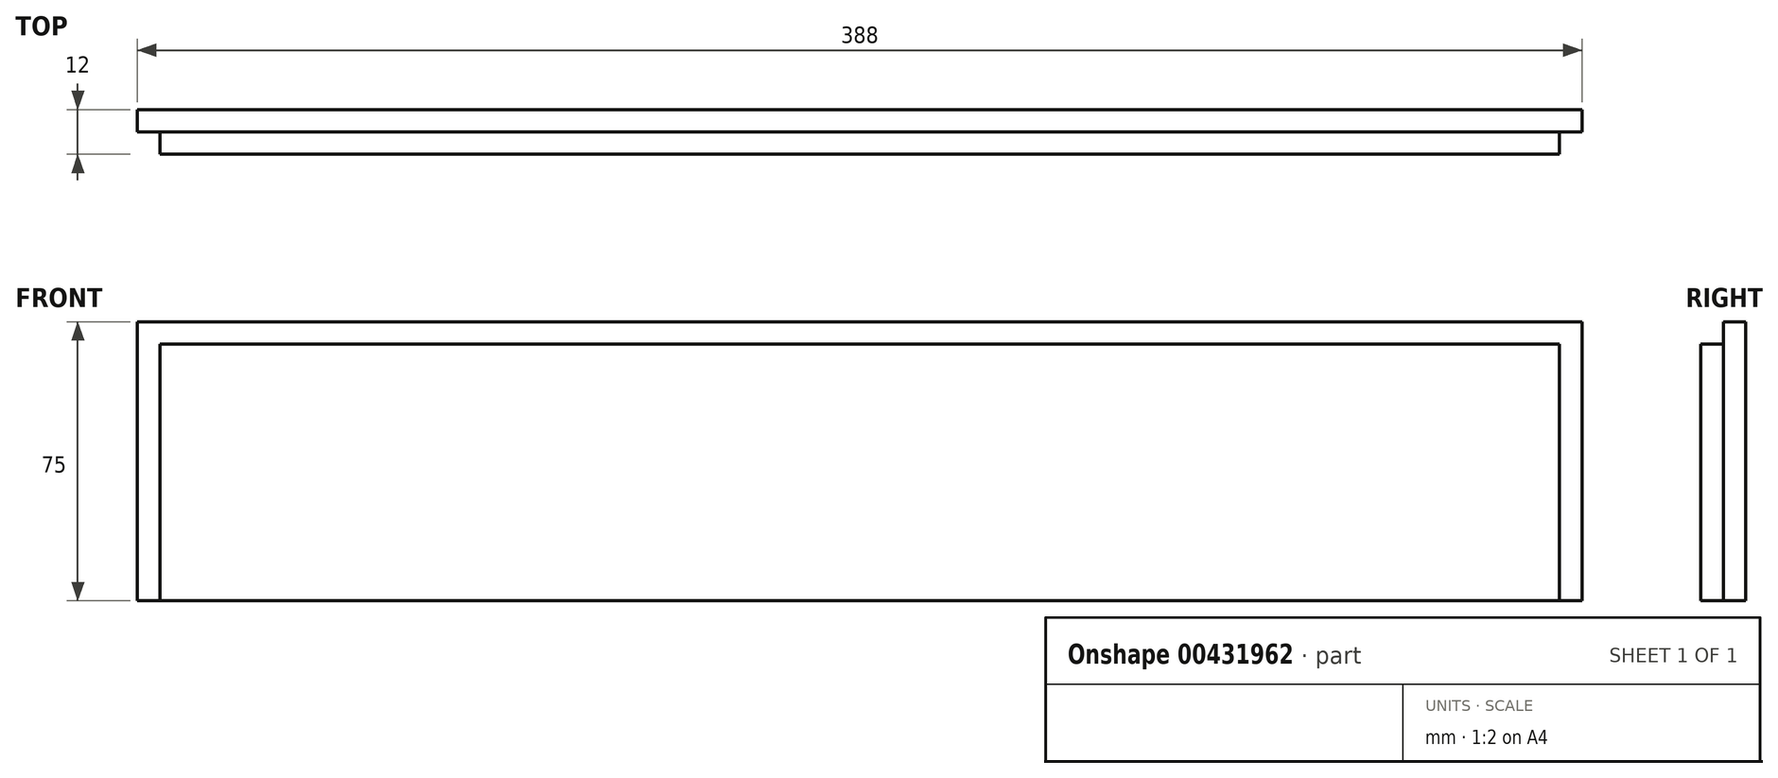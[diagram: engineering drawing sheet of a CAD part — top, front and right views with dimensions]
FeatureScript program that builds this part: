
annotation { "Feature Type Name" : "Feature", "Feature Type Description" : "" }
export const myFeature = defineFeature(function(context is Context, id is Id, definition is map)
    precondition{}
    {
        {
            var Q0;
            Q0=qCreatedBy(makeId("Front.planeOp"),FACE);
            var sketch = newSketch(context, id + "F0", { "sketchPlane" : qUnion([Q0])});
            skLineSegment(sketch, "E0.bottom", {"start": v(-183, 37.5) * mm, "end": v(205, 37.5) * mm});
            skLineSegment(sketch, "E0.top", {"start": v(-183, -37.5) * mm, "end": v(205, -37.5) * mm});
            skLineSegment(sketch, "E0.left", {"start": v(-183, 37.5) * mm, "end": v(-183, -37.5) * mm});
            skLineSegment(sketch, "E0.right", {"start": v(205, 37.5) * mm, "end": v(205, -37.5) * mm});
            skPoint(sketch, "E0.middle", {"position": v(11, 0) * mm});
            skSolve(sketch);
        }
        {
            var Q0;
            Q0=qSketchRegion(id+"F0",true);
            extrude(context, id + "F1", {"entities" : qUnion([Q0]), "depth" : 12 * mm, "offsetDistance" : 25 * mm});
        }
        {
            var Q0;
            Q0=makeQuery(id+"F1.opExtrude","CAP_FACE",FACE,{"disambiguationData":[OSD([sQuery(id+"F0.wireOp",EDGE,"E0.bottom"),sQuery(id+"F0.wireOp",EDGE,"E0.top"),sQuery(id+"F0.wireOp",EDGE,"E0.left"),sQuery(id+"F0.wireOp",EDGE,"E0.right")])],"isStart":false});
            var sketch = newSketch(context, id + "F2", { "sketchPlane" : qUnion([Q0])});
            skLineSegment(sketch, "E1.bottom", {"start": v(-183, 37.5) * mm, "end": v(-177, 37.5) * mm});
            skLineSegment(sketch, "E1.top", {"start": v(-183, -37.5) * mm, "end": v(-177, -37.5) * mm});
            skLineSegment(sketch, "E1.left", {"start": v(-183, 37.5) * mm, "end": v(-183, -37.5) * mm});
            skLineSegment(sketch, "E1.right", {"start": v(-177, 37.5) * mm, "end": v(-177, -37.5) * mm});
            skSolve(sketch);
        }
        {
            var Q0;
            Q0=qSketchRegion(id+"F2",true);
            extrude(context, id + "F3", {"entities" : qUnion([Q0]), "operationType" : NewBodyOperationType.REMOVE, "oppositeDirection" : true, "depth" : 6 * mm, "offsetDistance" : 25 * mm});
        }
        {
            var Q0;
            Q0=makeQuery(id+"F1.opExtrude","CAP_FACE",FACE,{"disambiguationData":[OSD([sQuery(id+"F0.wireOp",EDGE,"E0.bottom"),sQuery(id+"F0.wireOp",EDGE,"E0.top"),sQuery(id+"F0.wireOp",EDGE,"E0.left"),sQuery(id+"F0.wireOp",EDGE,"E0.right")])],"isStart":false});
            var sketch = newSketch(context, id + "F4", { "sketchPlane" : qUnion([Q0])});
            skLineSegment(sketch, "E2.bottom", {"start": v(205, 37.5) * mm, "end": v(199, 37.5) * mm});
            skLineSegment(sketch, "E2.top", {"start": v(205, -37.5) * mm, "end": v(199, -37.5) * mm});
            skLineSegment(sketch, "E2.left", {"start": v(205, 37.5) * mm, "end": v(205, -37.5) * mm});
            skLineSegment(sketch, "E2.right", {"start": v(199, 37.5) * mm, "end": v(199, -37.5) * mm});
            skSolve(sketch);
        }
        {
            var Q0;
            Q0=qSketchRegion(id+"F4",true);
            extrude(context, id + "F5", {"entities" : qUnion([Q0]), "operationType" : NewBodyOperationType.REMOVE, "oppositeDirection" : true, "depth" : 6 * mm, "offsetDistance" : 25 * mm});
        }
        {
            var Q0;
            Q0=makeQuery(id+"F1.opExtrude","CAP_FACE",FACE,{"disambiguationData":[OSD([sQuery(id+"F0.wireOp",EDGE,"E0.bottom"),sQuery(id+"F0.wireOp",EDGE,"E0.top"),sQuery(id+"F0.wireOp",EDGE,"E0.left"),sQuery(id+"F0.wireOp",EDGE,"E0.right")])],"isStart":false});
            var sketch = newSketch(context, id + "F6", { "sketchPlane" : qUnion([Q0])});
            skLineSegment(sketch, "E3.bottom", {"start": v(-177, 37.5) * mm, "end": v(199, 37.5) * mm});
            skLineSegment(sketch, "E3.top", {"start": v(-177, 31.5) * mm, "end": v(199, 31.5) * mm});
            skLineSegment(sketch, "E3.left", {"start": v(-177, 37.5) * mm, "end": v(-177, 31.5) * mm});
            skLineSegment(sketch, "E3.right", {"start": v(199, 37.5) * mm, "end": v(199, 31.5) * mm});
            skSolve(sketch);
        }
        {
            var Q0;
            Q0=qSketchRegion(id+"F6",true);
            extrude(context, id + "F7", {"entities" : qUnion([Q0]), "operationType" : NewBodyOperationType.REMOVE, "oppositeDirection" : true, "depth" : 6 * mm, "offsetDistance" : 25 * mm});
        }
    });
